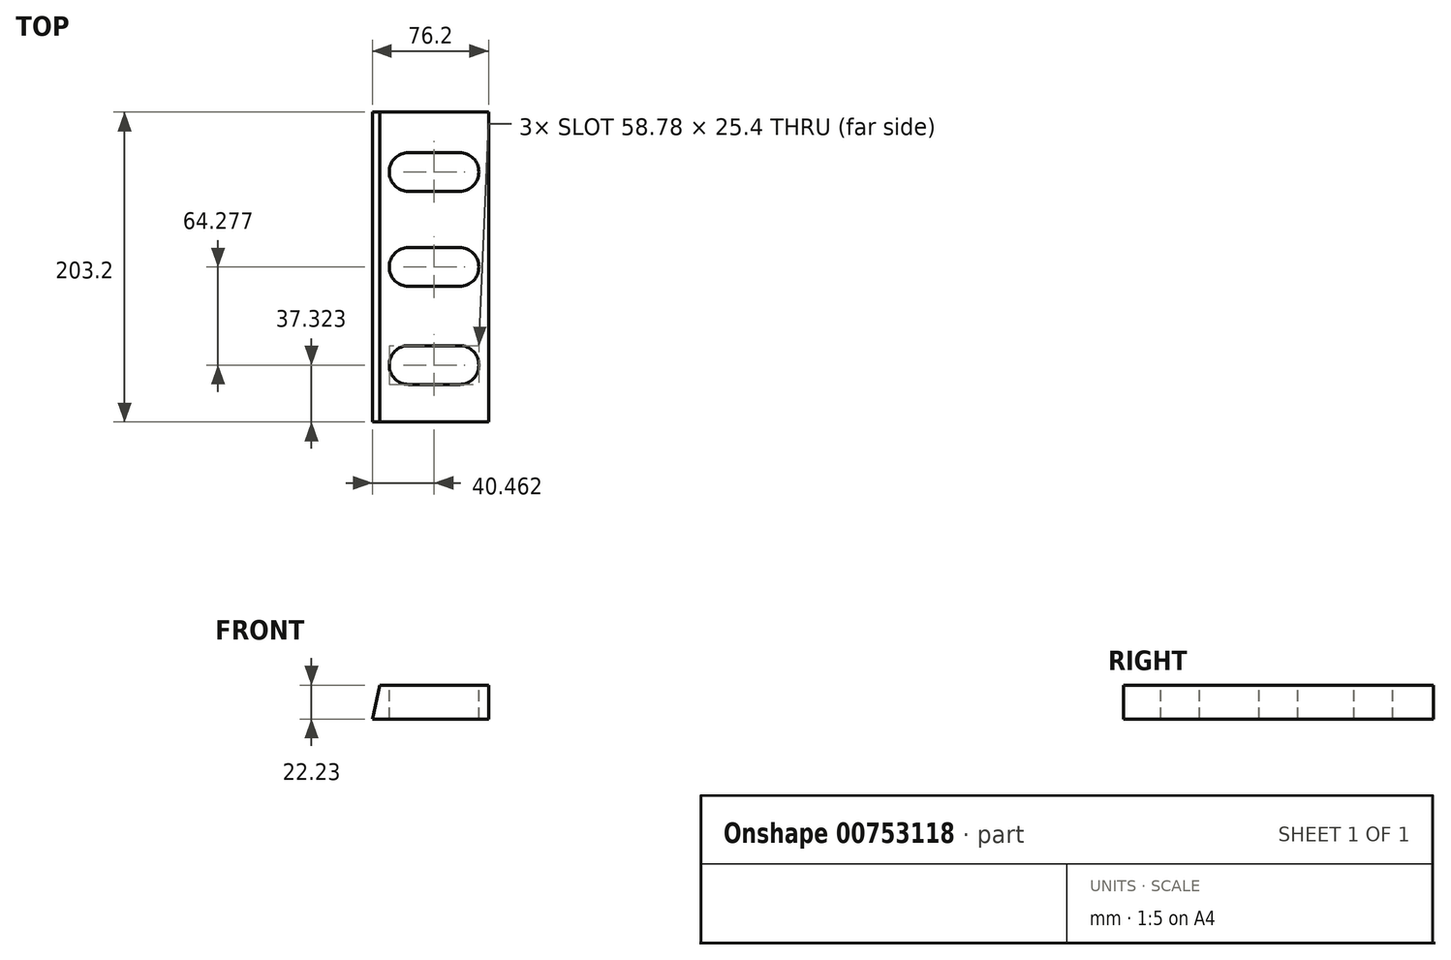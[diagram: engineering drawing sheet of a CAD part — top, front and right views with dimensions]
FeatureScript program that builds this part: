
annotation { "Feature Type Name" : "Feature", "Feature Type Description" : "" }
export const myFeature = defineFeature(function(context is Context, id is Id, definition is map)
    precondition{}
    {
        {
            var Q0;
            Q0=qCreatedBy(makeId("Front.planeOp"),FACE);
            var sketch = newSketch(context, id + "F0", { "sketchPlane" : qUnion([Q0])});
            skLineSegment(sketch, "E0", {"start": v(0, 0) * mm, "end": v(76.2, 0) * mm});
            skLineSegment(sketch, "E1", {"start": v(76.2, 0) * mm, "end": v(76.2, 22.23) * mm});
            skLineSegment(sketch, "E2", {"start": v(76.2, 22.22) * mm, "end": v(4.72, 22.22) * mm});
            skLineSegment(sketch, "E3", {"start": v(4.72, 22.22) * mm, "end": v(0, 0) * mm});
            skSolve(sketch);
        }
        {
            var Q0;
            Q0=makeQuery(id+"F0.imprint","IMPRINT",FACE,{"disambiguationData":[TD([[makeQuery(id+"F0.imprint","IMPRINT",EDGE,{"derivedFrom":sQuery(id+"F0.wireOp",EDGE,"E0")}),1.0]])]});
            extrude(context, id + "F1", {"entities" : qUnion([Q0]), "endBound" : BoundingType.SYMMETRIC, "depth" : 203.2 * mm, "offsetDistance" : 25.4 * mm});
        }
        {
            var Q0;
            Q0=makeQuery(id+"F1.opExtrude","SWEPT_FACE",FACE,{"disambiguationData":[OSD([sQuery(id+"F0.wireOp",EDGE,"E2")])]});
            var sketch = newSketch(context, id + "F2", { "sketchPlane" : qUnion([Q0])});
            skArc(sketch, "E4", {"start": v(23.77, 75.06) * mm, "mid": v(11.07, 62.36) * mm, "end": v(23.77, 49.66) * mm});
            skArc(sketch, "E5", {"start": v(57.15, 49.66) * mm, "mid": v(69.85, 62.36) * mm, "end": v(57.15, 75.06) * mm});
            skArc(sketch, "E6", {"start": v(23.77, 12.7) * mm, "mid": v(11.07, 0) * mm, "end": v(23.77, -12.7) * mm});
            skArc(sketch, "E7", {"start": v(57.15, -12.7) * mm, "mid": v(69.85, 0) * mm, "end": v(57.15, 12.7) * mm});
            skArc(sketch, "E8", {"start": v(23.77, -51.58) * mm, "mid": v(11.07, -64.28) * mm, "end": v(23.77, -76.98) * mm});
            skArc(sketch, "E9", {"start": v(57.15, -76.98) * mm, "mid": v(69.85, -64.28) * mm, "end": v(57.15, -51.58) * mm});
            skLineSegment(sketch, "E10", {"start": v(23.77, 75.06) * mm, "end": v(57.15, 75.06) * mm});
            skLineSegment(sketch, "E11", {"start": v(57.15, 49.66) * mm, "end": v(23.77, 49.66) * mm});
            skLineSegment(sketch, "E12", {"start": v(23.77, 12.7) * mm, "end": v(57.15, 12.7) * mm});
            skLineSegment(sketch, "E13", {"start": v(23.77, -12.7) * mm, "end": v(57.15, -12.7) * mm});
            skLineSegment(sketch, "E14", {"start": v(23.77, -51.58) * mm, "end": v(57.15, -51.58) * mm});
            skLineSegment(sketch, "E15", {"start": v(23.77, -76.98) * mm, "end": v(57.15, -76.98) * mm});
            skSolve(sketch);
        }
        {
            var Q0;
            Q0 = qSketchRegion(id + "F2", true);
            extrude(context, id + "F3", {"entities" : qUnion([Q0]), "operationType" : NewBodyOperationType.REMOVE, "oppositeDirection" : true, "depth" : 25.4 * mm, "offsetDistance" : 25.4 * mm});
        }
    });
